# Revit family: S-598_Horizontal
name_source: partatom
category: Aparatos sanitarios
revit_build: Autodesk Revit 2015 (Build: 20140606_1530(x64)
units: mm (PartAtom-declared; Revit-internal decimal feet)

## types (1)
- S-598_Horizontal_ABS Blanco
    Altura total mínima = 100 mm
    Caudal = 0.9 L/s
    Clase carga = K3
    Comentarios de tipo = CON PRENSATELAS PARA LÁMINAS IMPERMEABILIZANTES DE VINILO. CON TAPA DE PROTECCION DE OBRA
    Descripción = SUMIDERO PARA SUELOS DE VINILO, SIFON EXTRAIBLE, CON FILTRO DE PELOS, SALIDA HORIZONTAL, CON CAPO, ANTIVANDÁLICO, PLASTICO
    Diámetro = 50 mm  [stored 0.164042 ft]
    Fabricante = Jimten
    Material = ABS (Blanco)
    Medida = Ø160 mm
    Modelo = S-598
    Referencia = 12450
    Rejilla = ABS (Blanco)
    Salida = 50M
    Sello hidráulico = 50 mm
    URL = http://www.jimten.com
    WFU = 1

note: [stored X ft] marks values corroborated as IEEE doubles in the binary element streams (Revit-internal decimal feet)

## geometry (parser evidence)
native form markers: Blend x3, Sweep x9
no freeform markers — native parametric forms only
